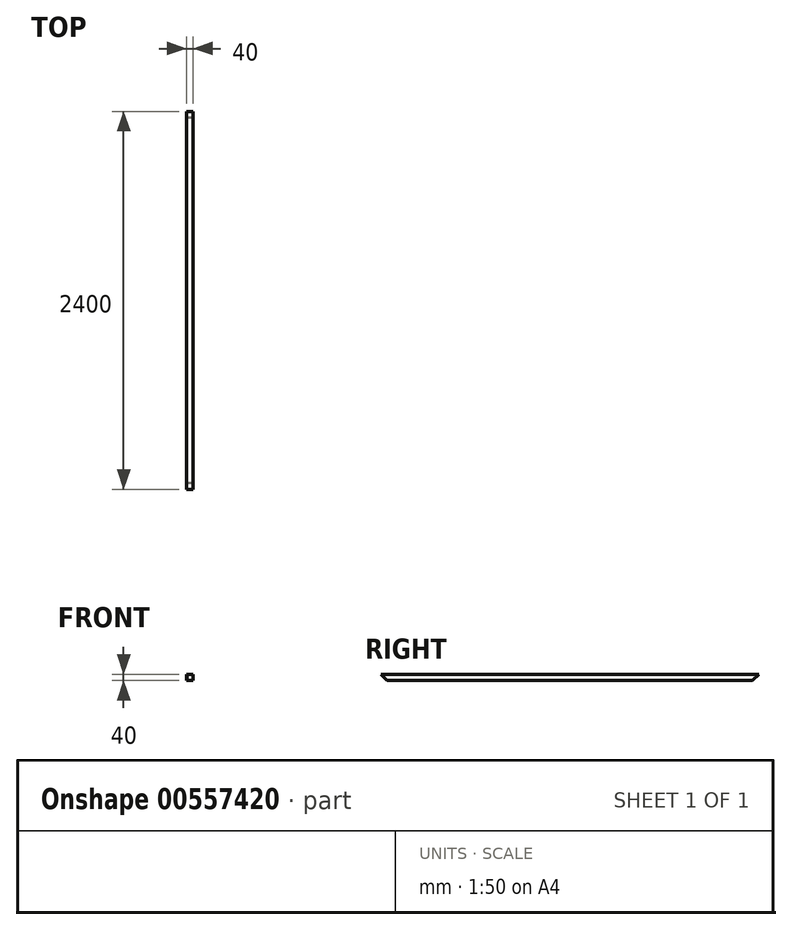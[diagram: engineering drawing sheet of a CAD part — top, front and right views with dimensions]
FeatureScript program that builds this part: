
annotation { "Feature Type Name" : "Feature", "Feature Type Description" : "" }
export const myFeature = defineFeature(function(context is Context, id is Id, definition is map)
    precondition{}
    {
        {
            var Q0;
            Q0=qCreatedBy(makeId("Front.planeOp"),FACE);
            var sketch = newSketch(context, id + "F0", { "sketchPlane" : qUnion([Q0])});
            skLineSegment(sketch, "E0.bottom", {"start": v(20, 20) * mm, "end": v(-20, 20) * mm});
            skLineSegment(sketch, "E0.top", {"start": v(20, -20) * mm, "end": v(-20, -20) * mm});
            skLineSegment(sketch, "E0.left", {"start": v(20, 20) * mm, "end": v(20, -20) * mm});
            skLineSegment(sketch, "E0.right", {"start": v(-20, 20) * mm, "end": v(-20, -20) * mm});
            skPoint(sketch, "E0.middle", {"position": v(0, 0) * mm});
            skLineSegment(sketch, "E1.0", {"start": v(-18.5, 18.5) * mm, "end": v(-18.5, -18.5) * mm});
            skLineSegment(sketch, "E1.1", {"start": v(18.5, 18.5) * mm, "end": v(-18.5, 18.5) * mm});
            skLineSegment(sketch, "E1.2", {"start": v(18.5, 18.5) * mm, "end": v(18.5, -18.5) * mm});
            skLineSegment(sketch, "E1.3", {"start": v(18.5, -18.5) * mm, "end": v(-18.5, -18.5) * mm});
            skSolve(sketch);
        }
        {
            var Q0;
            Q0=makeQuery(id+"F0.imprint","IMPRINT",FACE,{"disambiguationData":[TD([[makeQuery(id+"F0.imprint","IMPRINT",EDGE,{"derivedFrom":sQuery(id+"F0.wireOp",EDGE,"E0.bottom")}),1.0]])]});
            extrude(context, id + "F1", {"entities" : qUnion([Q0]), "endBound" : BoundingType.SYMMETRIC, "depth" : 2400 * mm, "offsetDistance" : 25 * mm});
        }
        {
            var Q0;
            Q0=makeQuery(id+"F1.opExtrude","SWEPT_FACE",FACE,{"disambiguationData":[OSD([sQuery(id+"F0.wireOp",EDGE,"E0.left")])]});
            var sketch = newSketch(context, id + "F2", { "sketchPlane" : qUnion([Q0])});
            skLineSegment(sketch, "E2", {"start": v(-1200, 20) * mm, "end": v(-1160, -20) * mm});
            skLineSegment(sketch, "E3", {"start": v(1200, 20) * mm, "end": v(1160, -20) * mm});
            skSolve(sketch);
        }
        {
            var Q0;
            {var subQ0=sQuery(id+"F2.wireOp",EDGE,"E3");Q0=makeQuery(id+"F2.imprint","IMPRINT",FACE,{"disambiguationData":[TD([[makeQuery(id+"F2.imprint","IMPRINT",EDGE,{"derivedFrom":subQ0}),1.0]])]});}
            var Q1;
            {var subQ0=sQuery(id+"F2.wireOp",EDGE,"E2");Q1=makeQuery(id+"F2.imprint","IMPRINT",FACE,{"disambiguationData":[TD([[makeQuery(id+"F2.imprint","IMPRINT",EDGE,{"derivedFrom":subQ0}),-1.0]])]});}
            extrude(context, id + "F3", {"entities" : qUnion([Q0, Q1]), "operationType" : NewBodyOperationType.REMOVE, "oppositeDirection" : true, "depth" : 40 * mm, "offsetDistance" : 25 * mm});
        }
    });
